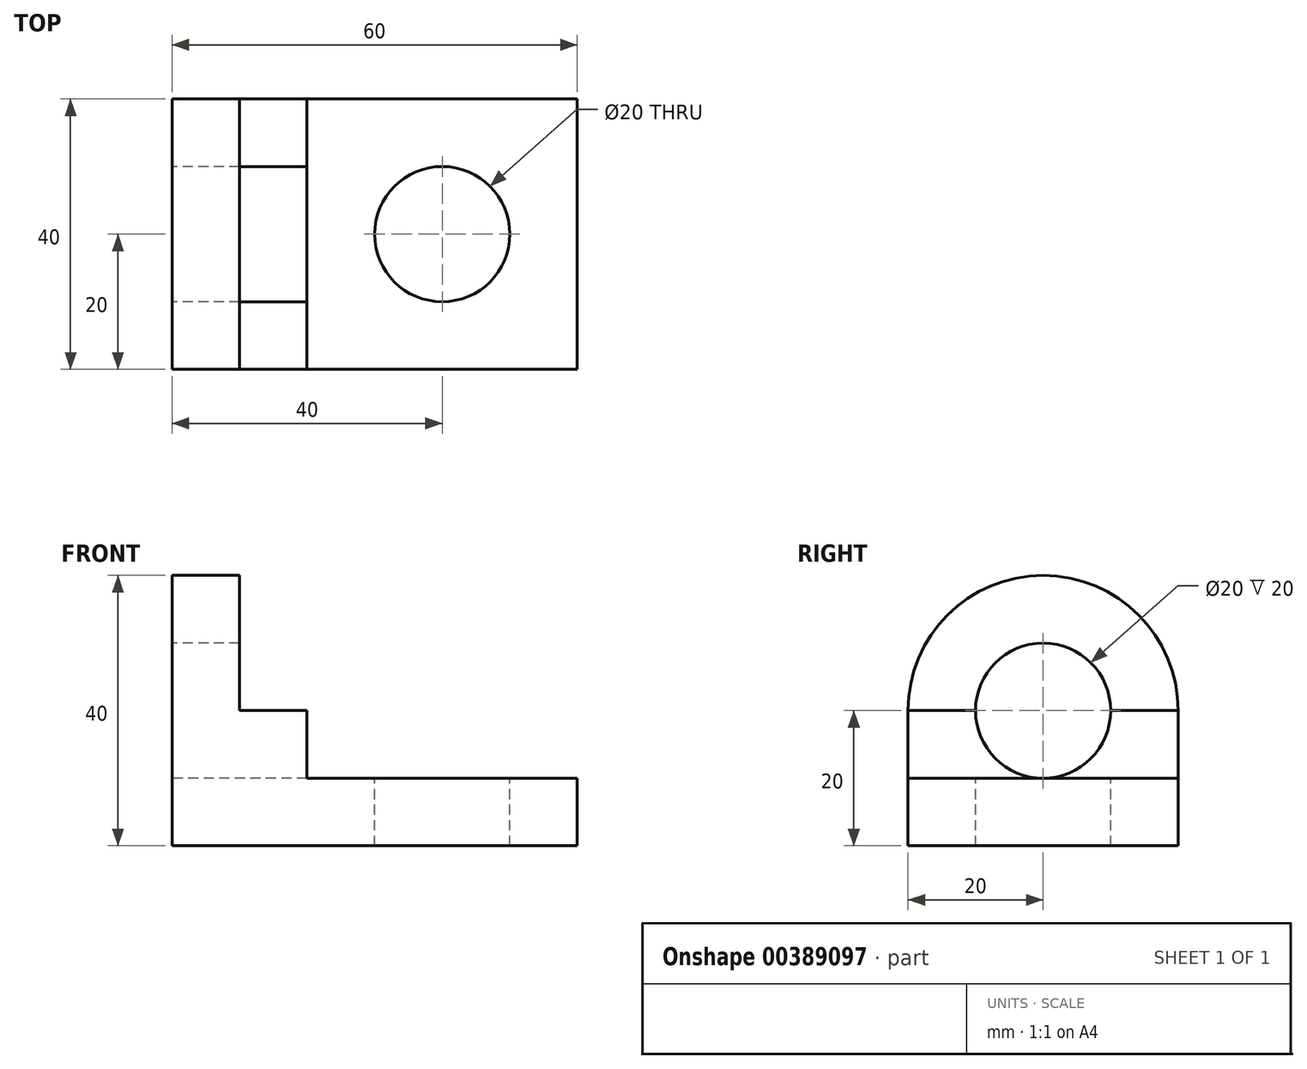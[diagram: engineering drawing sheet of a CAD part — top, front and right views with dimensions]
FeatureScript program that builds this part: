
annotation { "Feature Type Name" : "Feature", "Feature Type Description" : "" }
export const myFeature = defineFeature(function(context is Context, id is Id, definition is map)
    precondition{}
    {
        {
            var Q0;
            Q0=qCreatedBy(makeId("Top.planeOp"),FACE);
            var sketch = newSketch(context, id + "F0", { "sketchPlane" : qUnion([Q0])});
            skLineSegment(sketch, "E0.bottom", {"start": v(-30, 20) * mm, "end": v(30, 20) * mm});
            skLineSegment(sketch, "E0.top", {"start": v(-30, -20) * mm, "end": v(30, -20) * mm});
            skLineSegment(sketch, "E0.left", {"start": v(-30, 20) * mm, "end": v(-30, -20) * mm});
            skLineSegment(sketch, "E0.right", {"start": v(30, 20) * mm, "end": v(30, -20) * mm});
            skPoint(sketch, "E0.middle", {"position": v(0, 0) * mm});
            skSolve(sketch);
        }
        {
            var Q0;
            Q0 = qSketchRegion(id + "F0", true);
            extrude(context, id + "F1", {"entities" : qUnion([Q0]), "depth" : 10 * mm});
        }
        {
            var Q0;
            Q0=makeQuery(id+"F1.opExtrude","CAP_FACE",FACE,{"disambiguationData":[OSD([sQuery(id+"F0.wireOp",EDGE,"E0.bottom"),sQuery(id+"F0.wireOp",EDGE,"E0.top"),sQuery(id+"F0.wireOp",EDGE,"E0.left"),sQuery(id+"F0.wireOp",EDGE,"E0.right")])],"isStart":false});
            var sketch = newSketch(context, id + "F2", { "sketchPlane" : qUnion([Q0])});
            skLineSegment(sketch, "E1.bottom", {"start": v(-30, 20) * mm, "end": v(-20, 20) * mm});
            skLineSegment(sketch, "E1.top", {"start": v(-30, -20) * mm, "end": v(-20, -20) * mm});
            skLineSegment(sketch, "E1.left", {"start": v(-30, 20) * mm, "end": v(-30, -20) * mm});
            skLineSegment(sketch, "E1.right", {"start": v(-20, 20) * mm, "end": v(-20, -20) * mm});
            skSolve(sketch);
        }
        {
            var Q0;
            Q0 = qSketchRegion(id + "F2", true);
            extrude(context, id + "F3", {"entities" : qUnion([Q0]), "operationType" : NewBodyOperationType.ADD, "depth" : 30 * mm});
        }
        {
            var Q0;
            Q0=makeQuery(id+"F1.opExtrude","CAP_FACE",FACE,{"disambiguationData":[OSD([sQuery(id+"F0.wireOp",EDGE,"E0.bottom"),sQuery(id+"F0.wireOp",EDGE,"E0.top"),sQuery(id+"F0.wireOp",EDGE,"E0.left"),sQuery(id+"F0.wireOp",EDGE,"E0.right")])],"isStart":false});
            var sketch = newSketch(context, id + "F4", { "sketchPlane" : qUnion([Q0])});
            skLineSegment(sketch, "E2.bottom", {"start": v(-20, -20) * mm, "end": v(-10, -20) * mm});
            skLineSegment(sketch, "E2.top", {"start": v(-20, 20) * mm, "end": v(-10, 20) * mm});
            skLineSegment(sketch, "E2.left", {"start": v(-20, -20) * mm, "end": v(-20, 20) * mm});
            skLineSegment(sketch, "E2.right", {"start": v(-10, -20) * mm, "end": v(-10, 20) * mm});
            skSolve(sketch);
        }
        {
            var Q0;
            Q0 = qSketchRegion(id + "F4", true);
            extrude(context, id + "F5", {"entities" : qUnion([Q0]), "operationType" : NewBodyOperationType.ADD, "depth" : 10 * mm});
        }
        {
            var Q0;
            Q0=makeQuery(id+"F3.boolean.opBoolean","MERGE",FACE,{"derivedFrom":[makeQuery(id+"F1.opExtrude","SWEPT_FACE",FACE,{"disambiguationData":[OSD([sQuery(id+"F0.wireOp",EDGE,"E0.left")])]}),makeQuery(id+"F3.opExtrude","SWEPT_FACE",FACE,{"disambiguationData":[OSD([sQuery(id+"F2.wireOp",EDGE,"E1.left")])]})]});
            var sketch = newSketch(context, id + "F6", { "sketchPlane" : qUnion([Q0])});
            skCircle(sketch, "E3", {"center": v(0, 20) * mm, "radius": 10 * mm});
            skSolve(sketch);
        }
        {
            var Q0;
            Q0=makeQuery(id+"F6.imprint","IMPRINT",FACE,{"disambiguationData":[TD([[makeQuery(id+"F6.imprint","IMPRINT",EDGE,{"derivedFrom":sQuery(id+"F6.wireOp",EDGE,"E3")}),1.0]])]});
            extrude(context, id + "F7", {"entities" : qUnion([Q0]), "operationType" : NewBodyOperationType.REMOVE, "endBound" : BoundingType.THROUGH_ALL, "oppositeDirection" : true, "depth" : 25.4 * mm});
        }
        {
            var Q0;
            Q0=makeQuery(id+"F3.opExtrude","CAP_EDGE",EDGE,{"disambiguationData":[OSD([sQuery(id+"F2.wireOp",EDGE,"E1.top")])],"isStart":false});
            fillet(context, id + "F8", {"entities" : qUnion([Q0]), "radius" : 20 * mm, "tangentPropagation" : true, "allowEdgeOverflow" : false});
        }
        {
            var Q0;
            Q0=makeQuery(id+"F3.opExtrude","CAP_EDGE",EDGE,{"disambiguationData":[OSD([sQuery(id+"F2.wireOp",EDGE,"E1.bottom")])],"isStart":false});
            fillet(context, id + "F9", {"entities" : qUnion([Q0]), "radius" : 20 * mm, "tangentPropagation" : true, "allowEdgeOverflow" : false});
        }
        {
            var Q0;
            Q0=makeQuery(id+"F1.opExtrude","CAP_FACE",FACE,{"disambiguationData":[OSD([sQuery(id+"F0.wireOp",EDGE,"E0.bottom"),sQuery(id+"F0.wireOp",EDGE,"E0.top"),sQuery(id+"F0.wireOp",EDGE,"E0.left"),sQuery(id+"F0.wireOp",EDGE,"E0.right")])],"isStart":false});
            var sketch = newSketch(context, id + "F10", { "sketchPlane" : qUnion([Q0])});
            skCircle(sketch, "E4", {"center": v(10, 0) * mm, "radius": 10 * mm});
            skSolve(sketch);
        }
        {
            var Q0;
            Q0=makeQuery(id+"F10.imprint","IMPRINT",FACE,{"disambiguationData":[TD([[makeQuery(id+"F10.imprint","IMPRINT",EDGE,{"derivedFrom":sQuery(id+"F10.wireOp",EDGE,"E4")}),1.0]])]});
            extrude(context, id + "F11", {"entities" : qUnion([Q0]), "operationType" : NewBodyOperationType.REMOVE, "endBound" : BoundingType.THROUGH_ALL, "oppositeDirection" : true, "depth" : 25.4 * mm});
        }
    });
